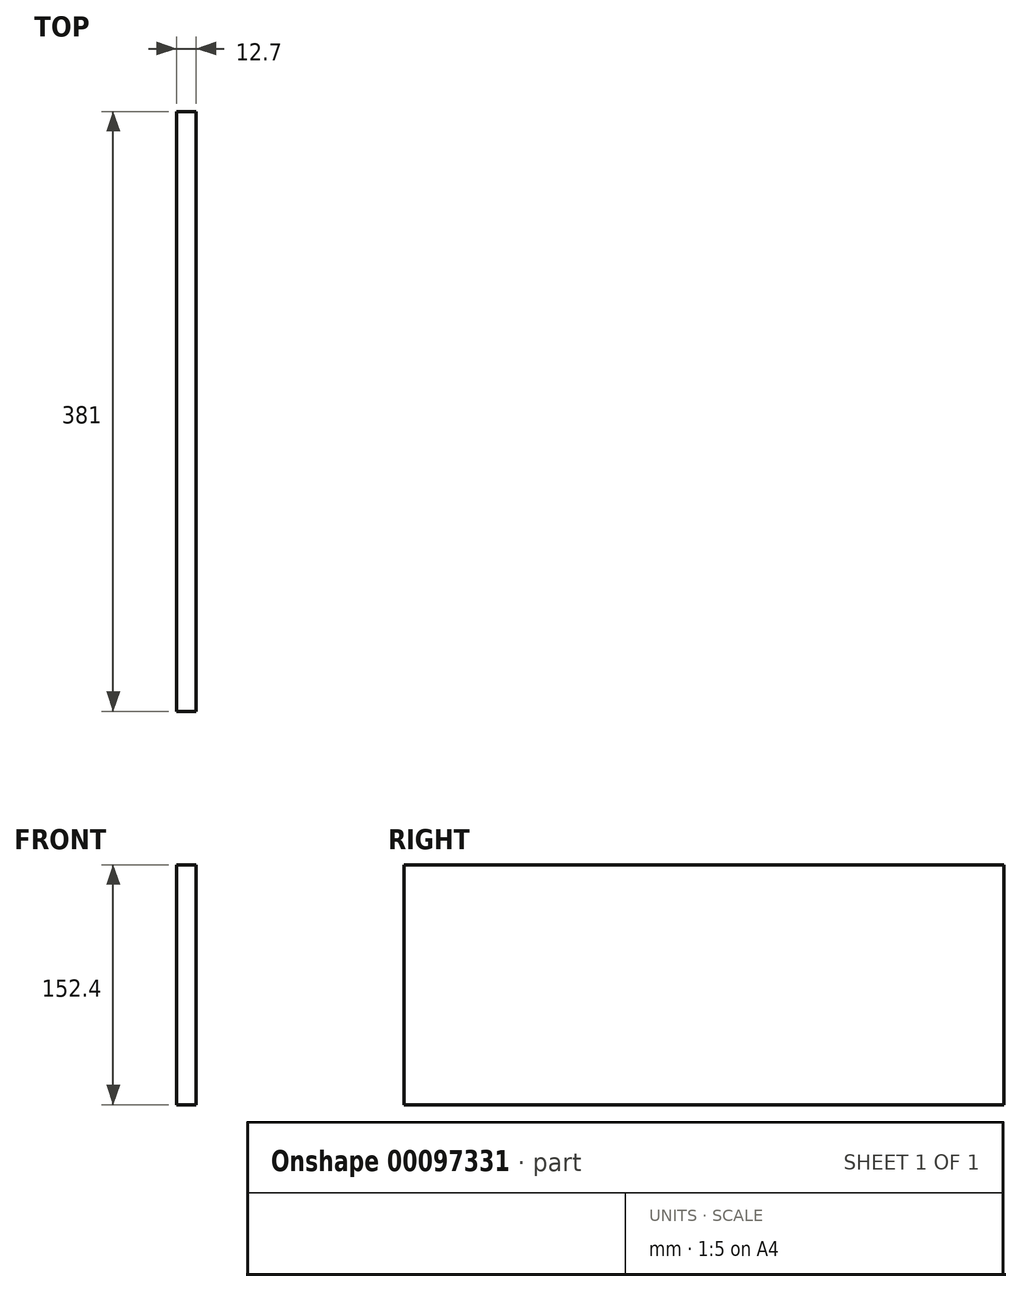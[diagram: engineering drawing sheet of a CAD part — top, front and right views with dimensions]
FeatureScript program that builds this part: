
annotation { "Feature Type Name" : "Feature", "Feature Type Description" : "" }
export const myFeature = defineFeature(function(context is Context, id is Id, definition is map)
    precondition{}
    {
        {
            var Q0;
            Q0=qCreatedBy(makeId("Right.planeOp"),FACE);
            var sketch = newSketch(context, id + "F0", { "sketchPlane" : qUnion([Q0])});
            skLineSegment(sketch, "E0.bottom", {"start": v(190.5, 76.2) * mm, "end": v(-190.5, 76.2) * mm});
            skLineSegment(sketch, "E0.top", {"start": v(190.5, -76.2) * mm, "end": v(-190.5, -76.2) * mm});
            skLineSegment(sketch, "E0.left", {"start": v(190.5, 76.2) * mm, "end": v(190.5, -76.2) * mm});
            skLineSegment(sketch, "E0.right", {"start": v(-190.5, 76.2) * mm, "end": v(-190.5, -76.2) * mm});
            skPoint(sketch, "E0.middle", {"position": v(0, 0) * mm});
            skSolve(sketch);
        }
        {
            var Q0;
            Q0=makeQuery(id+"F0.imprint","IMPRINT",FACE,{"disambiguationData":[TD([[makeQuery(id+"F0.imprint","IMPRINT",EDGE,{"derivedFrom":sQuery(id+"F0.wireOp",EDGE,"E0.bottom")}),1.0]])]});
            extrude(context, id + "F1", {"entities" : qUnion([Q0]), "depth" : 12.7 * mm});
        }
    });
